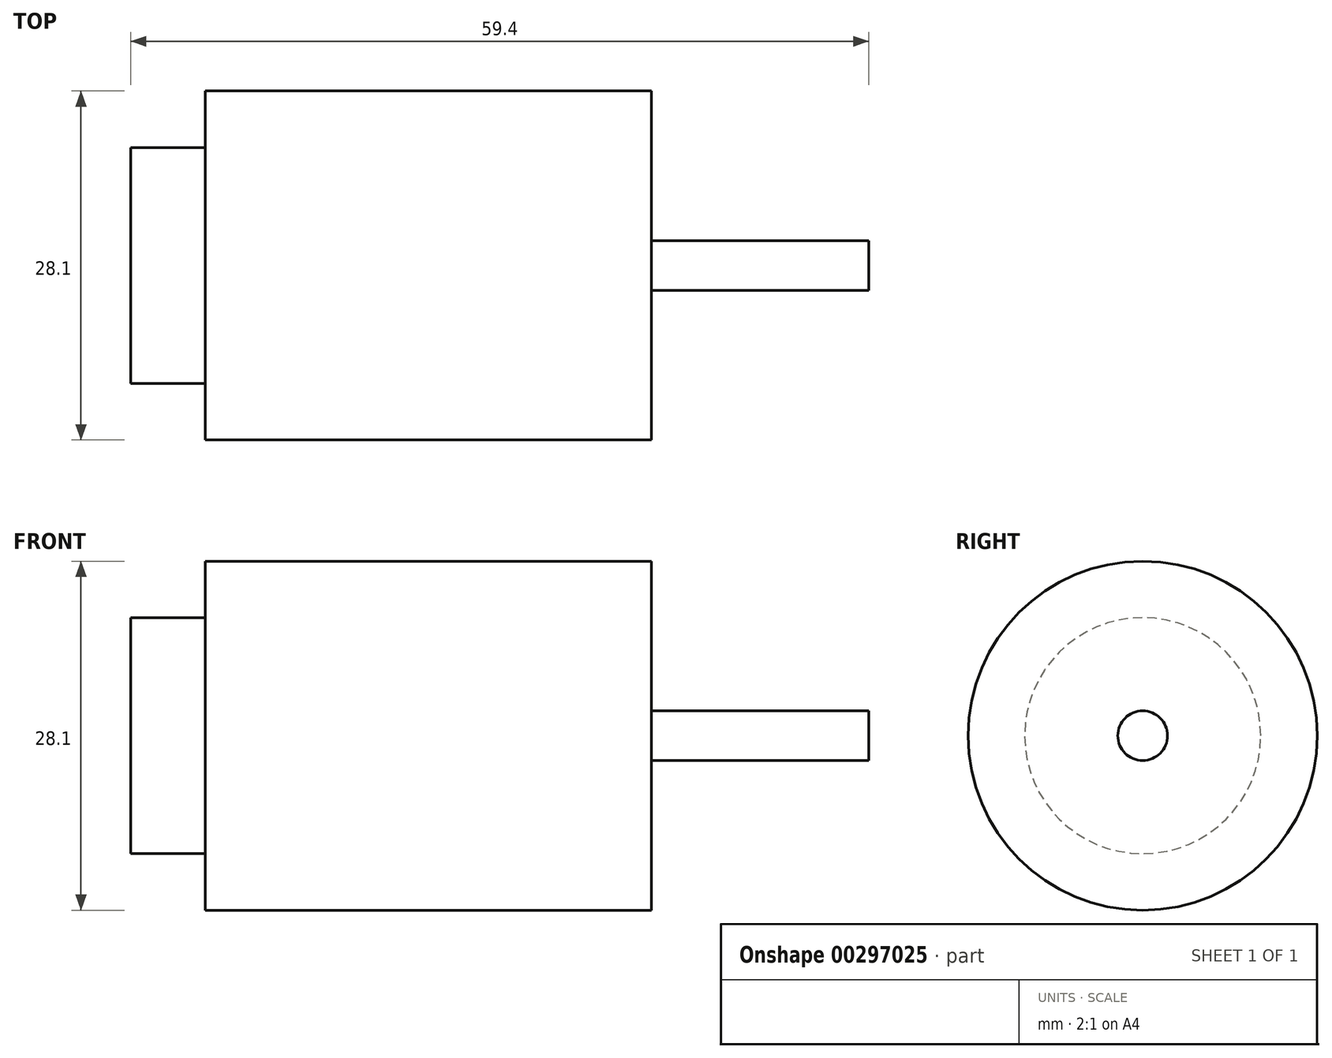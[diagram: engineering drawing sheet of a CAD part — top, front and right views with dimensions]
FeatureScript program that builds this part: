
annotation { "Feature Type Name" : "Feature", "Feature Type Description" : "" }
export const myFeature = defineFeature(function(context is Context, id is Id, definition is map)
    precondition{}
    {
        {
            var Q0;
            Q0=qCreatedBy(makeId("Front.planeOp"),FACE);
            var sketch = newSketch(context, id + "F0", { "sketchPlane" : qUnion([Q0])});
            skLineSegment(sketch, "E0.bottom", {"start": v(-35.9, 14.05) * mm, "end": v(0, 14.05) * mm});
            skLineSegment(sketch, "E0.top", {"start": v(-35.9, -14.05) * mm, "end": v(0, -14.05) * mm});
            skLineSegment(sketch, "E0.left", {"start": v(-35.9, 14.05) * mm, "end": v(-35.9, -14.05) * mm});
            skLineSegment(sketch, "E0.right", {"start": v(0, 14.05) * mm, "end": v(0, -14.05) * mm});
            skLineSegment(sketch, "E1.bottom", {"start": v(-41.9, -9.5) * mm, "end": v(-35.9, -9.5) * mm});
            skLineSegment(sketch, "E1.top", {"start": v(-41.9, 9.5) * mm, "end": v(-35.9, 9.5) * mm});
            skLineSegment(sketch, "E1.left", {"start": v(-41.9, 9.5) * mm, "end": v(-41.9, -9.5) * mm});
            skLineSegment(sketch, "E1.right", {"start": v(-35.9, 9.5) * mm, "end": v(-35.9, -9.5) * mm});
            skLineSegment(sketch, "E2", {"start": v(0, 0) * mm, "end": v(-41.9, 0) * mm});
            skLineSegment(sketch, "E3.bottom", {"start": v(0, -2) * mm, "end": v(17.5, -2) * mm});
            skLineSegment(sketch, "E3.top", {"start": v(0, 2) * mm, "end": v(17.5, 2) * mm});
            skLineSegment(sketch, "E3.left", {"start": v(0, 2) * mm, "end": v(0, -2) * mm});
            skLineSegment(sketch, "E3.right", {"start": v(17.5, 2) * mm, "end": v(17.5, -2) * mm});
            skLineSegment(sketch, "E4", {"start": v(0, 0) * mm, "end": v(17.5, 0) * mm});
            skSolve(sketch);
        }
        {
            var Q0;
            {var subQ1=sQuery(id+"F0.wireOp",EDGE,"E0.bottom");Q0=makeQuery(id+"F0.imprint","IMPRINT",FACE,{"disambiguationData":[TD([[makeQuery(id+"F0.imprint","IMPRINT",EDGE,{"derivedFrom":subQ1}),-1.0]])]});}
            var Q1;
            {var subQ0=sQuery(id+"F0.wireOp",EDGE,"E1.top");Q1=makeQuery(id+"F0.imprint","IMPRINT",FACE,{"disambiguationData":[TD([[makeQuery(id+"F0.imprint","IMPRINT",EDGE,{"derivedFrom":subQ0}),-1.0]])]});}
            var Q2;
            {var subQ0=sQuery(id+"F0.wireOp",EDGE,"E3.top");Q2=makeQuery(id+"F0.imprint","IMPRINT",FACE,{"disambiguationData":[TD([[makeQuery(id+"F0.imprint","IMPRINT",EDGE,{"derivedFrom":subQ0}),-1.0]])]});}
            var Q3;
            Q3=sQuery(id+"F0.wireOp",EDGE,"E2");
            revolve(context, id + "F1", {"entities" : qUnion([Q0, Q1, Q2]), "axis" : qUnion([Q3]), "revolveType" : RevolveType.FULL});
        }
    });
